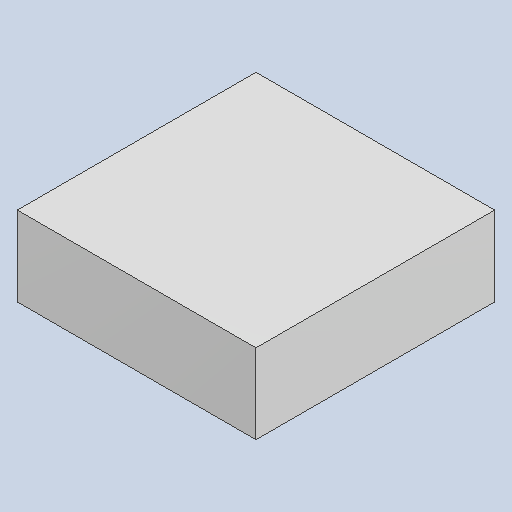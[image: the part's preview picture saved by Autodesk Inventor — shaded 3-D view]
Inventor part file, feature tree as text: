
AUTODESK INVENTOR PART (.ipt)
format: ipt  version: 2023.4 (Build 274418000, 418)  size: 79,872 bytes
history: native  units: mm
features: extrude x1
ambient origin geometry x8: Origin, YZ Plane, XZ Plane, XY Plane, X Axis, Y Axis, Z Axis, Center Point
bodies: Solid1 (feature_tree)
feature tree (1):
  extrude  "Extruded_54"  [1 undecoded]
note: 1 required parameter value undecoded (feature->parameter linkage not recoverable at this tier; creation-order binding heuristic only, values carry confidence <= 0.55)
